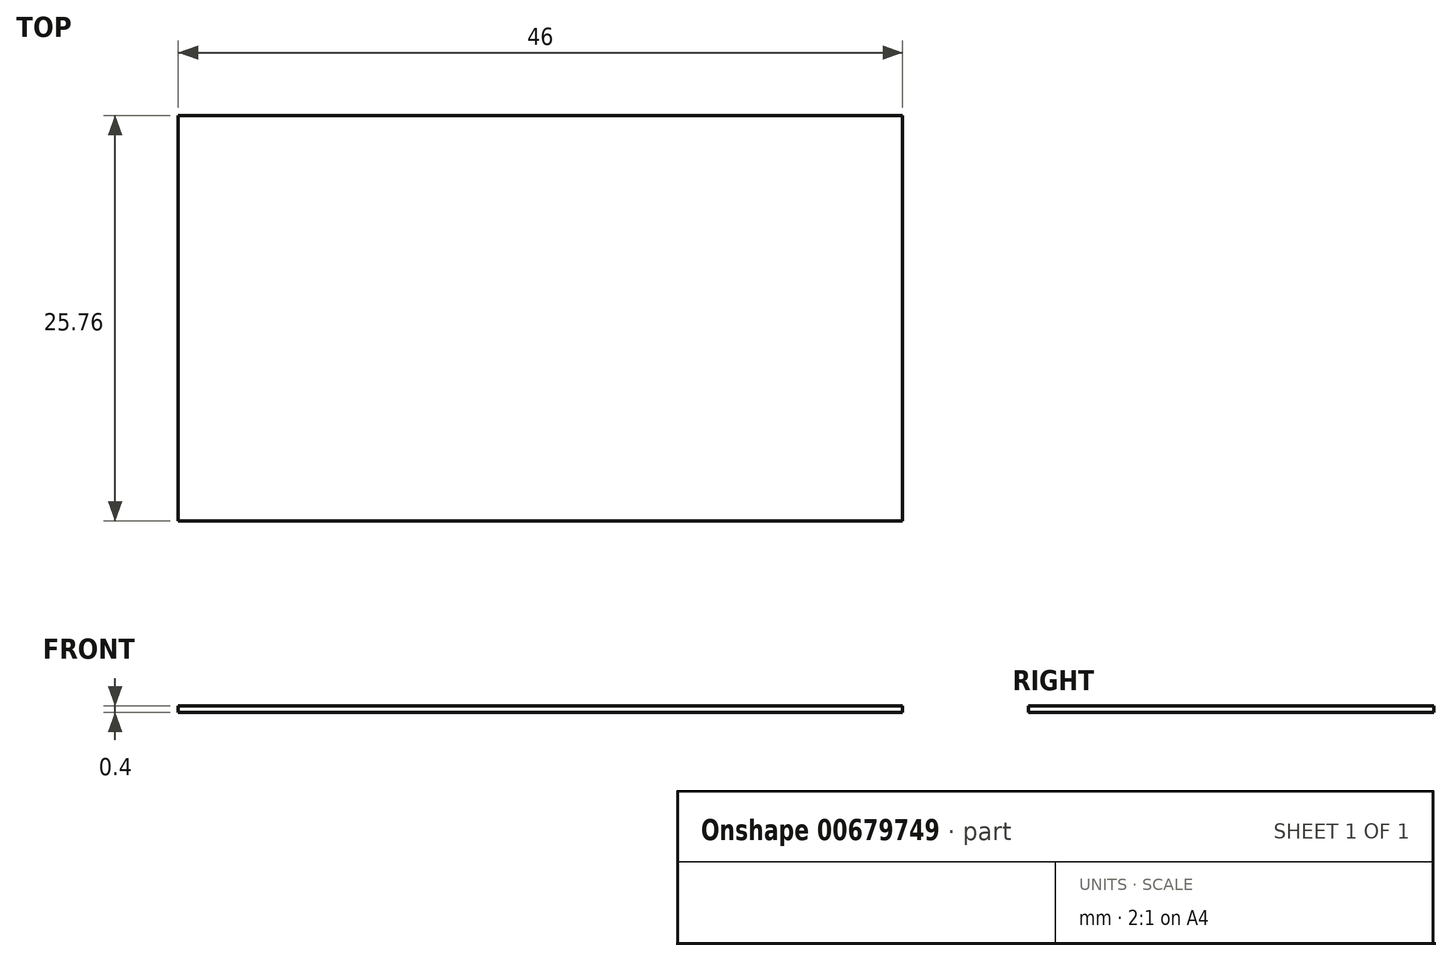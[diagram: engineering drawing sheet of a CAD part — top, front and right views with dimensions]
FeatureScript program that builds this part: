
annotation { "Feature Type Name" : "Feature", "Feature Type Description" : "" }
export const myFeature = defineFeature(function(context is Context, id is Id, definition is map)
    precondition{}
    {
        {
            var Q0;
            Q0=qCreatedBy(makeId("Top.planeOp"),FACE);
            var sketch = newSketch(context, id + "F0", { "sketchPlane" : qUnion([Q0])});
            skLineSegment(sketch, "E0.bottom", {"start": v(-23, 12.88) * mm, "end": v(23, 12.88) * mm});
            skLineSegment(sketch, "E0.top", {"start": v(-23, -12.88) * mm, "end": v(23, -12.88) * mm});
            skLineSegment(sketch, "E0.left", {"start": v(-23, 12.88) * mm, "end": v(-23, -12.88) * mm});
            skLineSegment(sketch, "E0.right", {"start": v(23, 12.88) * mm, "end": v(23, -12.88) * mm});
            skSolve(sketch);
        }
        {
            var Q0;
            Q0=makeQuery(id+"F0.imprint","IMPRINT",FACE,{"disambiguationData":[TD([[makeQuery(id+"F0.imprint","IMPRINT",EDGE,{"derivedFrom":sQuery(id+"F0.wireOp",EDGE,"E0.bottom")}),-1.0]])]});
            extrude(context, id + "F1", {"entities" : qUnion([Q0]), "depth" : .4 * mm, "offsetDistance" : 25 * mm});
        }
    });
